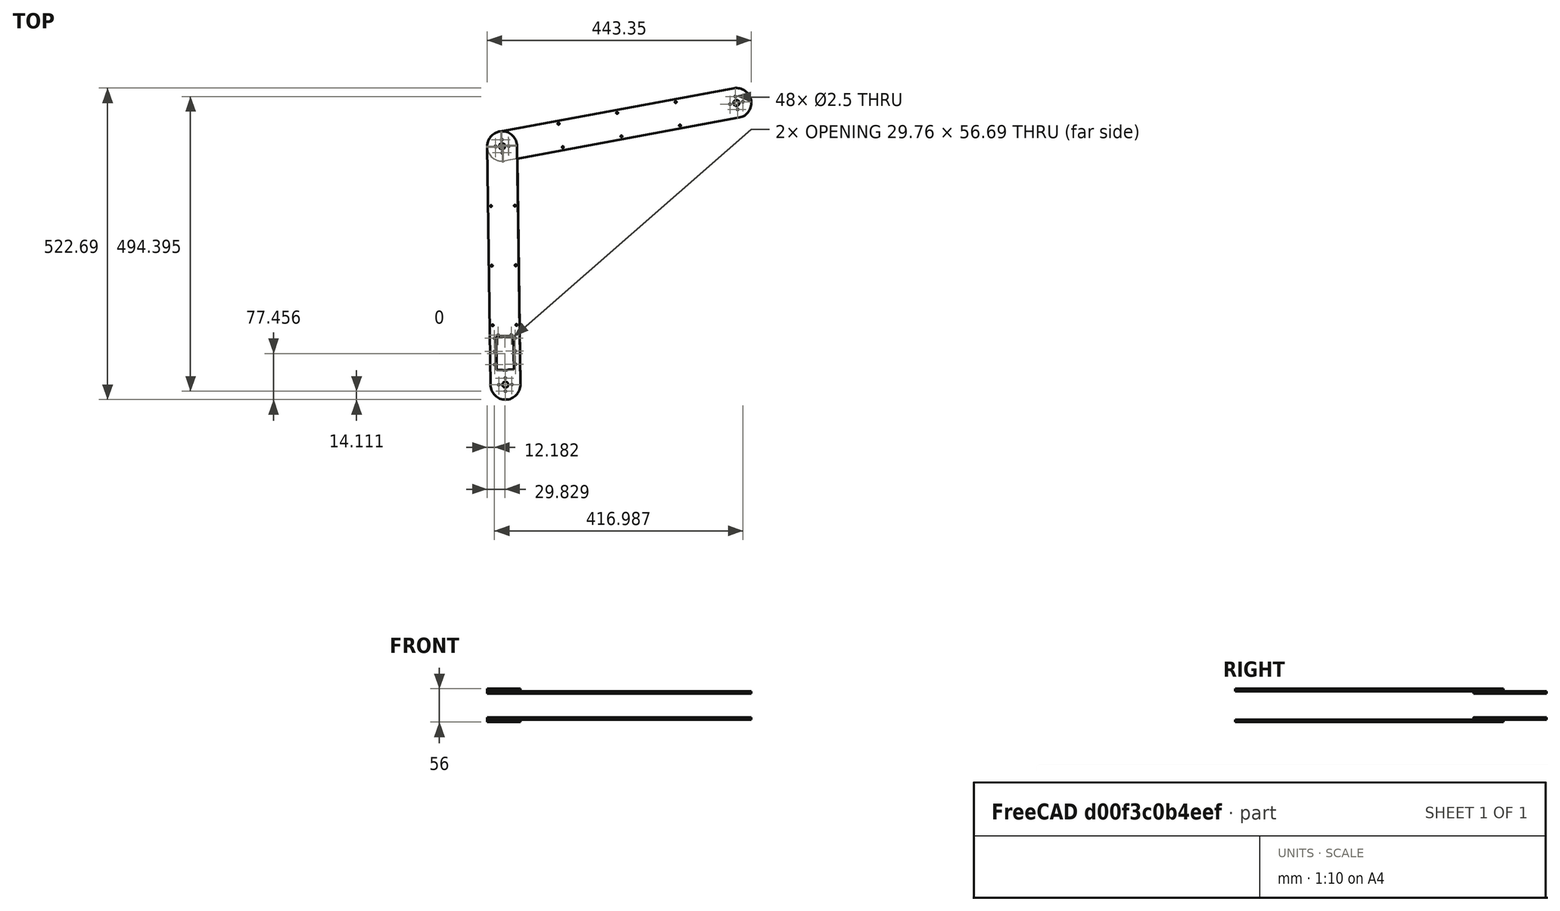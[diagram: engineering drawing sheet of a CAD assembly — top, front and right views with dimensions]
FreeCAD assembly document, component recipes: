
FREECAD ASSEMBLY — COMPONENT RECIPES ("arm_assembly_def")

This assembly document has 14 components, labeled P0..P13 below (a component is one placed body or linked part). 10 of them carry a construction recipe — the FreeCAD feature program that regenerates the part from scratch, quoted from this document or its linked companion documents; the rest are supplied as boundary geometry only. No exploded tour is included for this assembly.
COMPONENT P0 — recipe-attached ("arm_low_1", modeled in this document).
Construction recipe (the document's own serialized feature program — sketch geometry with constraints, then the solid features built on it; lengths are millimeters unless a unit is written):

FEATURE [Sketcher::SketchObject] Sketch
  ArcFitTolerance = 1e-06
  AttachmentSupport = -> [XY_Plane]
  FullyConstrained = false
  MakeInternals = false
  MapMode = 5
  sketch-geometry (67):
    g0: LineSegment [constr] StartX=1.5008e-12 StartY=20 StartZ=0 EndX=1.5008e-12 EndY=-20 EndZ=0
    g1: LineSegment [constr] StartX=-2.359e-12 StartY=0 StartZ=0 EndX=-2.359e-12 EndY=400 EndZ=0
    g2: LineSegment [constr] StartX=1.5008e-12 StartY=20 StartZ=0 EndX=1.5008e-12 EndY=25 EndZ=0
    g3: Circle CenterX=-2.359e-12 CenterY=400 CenterZ=0 NormalX=0 NormalY=0 NormalZ=1 AngleXU=0 Radius=5
    g4: Circle CenterX=-2.359e-12 CenterY=400 CenterZ=0 NormalX=0 NormalY=0 NormalZ=1 AngleXU=0 Radius=2
    g5: Circle CenterX=-10.9997 CenterY=400 CenterZ=0 NormalX=0 NormalY=0 NormalZ=1 AngleXU=0 Radius=1.25
    g6: Circle CenterX=0 CenterY=389 CenterZ=0 NormalX=0 NormalY=0 NormalZ=1 AngleXU=0 Radius=1.25
    g7: Circle CenterX=10.9997 CenterY=400 CenterZ=0 NormalX=0 NormalY=0 NormalZ=1 AngleXU=0 Radius=1.25
    g8: Circle CenterX=0 CenterY=411 CenterZ=0 NormalX=0 NormalY=0 NormalZ=1 AngleXU=0 Radius=1.25
    g9: LineSegment [constr] StartX=0 StartY=-5 StartZ=0 EndX=0 EndY=5.99996 EndZ=0
    g10: Circle [constr] CenterX=0 CenterY=0 CenterZ=0 NormalX=0 NormalY=0 NormalZ=1 AngleXU=0 Radius=14
    g11: LineSegment [constr] StartX=0 StartY=0 StartZ=0 EndX=25.23 EndY=0 EndZ=0
    g12: Circle [constr] CenterX=0 CenterY=-3.8e-05 CenterZ=0 NormalX=0 NormalY=0 NormalZ=1 AngleXU=0 Radius=11
    g13: Circle CenterX=0 CenterY=0 CenterZ=0 NormalX=0 NormalY=0 NormalZ=1 AngleXU=0 Radius=5
    g14: Circle CenterX=10.9997 CenterY=0 CenterZ=0 NormalX=0 NormalY=0 NormalZ=1 AngleXU=0 Radius=1.25
    g15: Circle CenterX=-10.9997 CenterY=0 CenterZ=0 NormalX=0 NormalY=0 NormalZ=1 AngleXU=0 Radius=1.25
    g16: Circle CenterX=0 CenterY=-10.9997 CenterZ=0 NormalX=0 NormalY=0 NormalZ=1 AngleXU=0 Radius=1.25
    g17: Circle CenterX=0 CenterY=11 CenterZ=0 NormalX=0 NormalY=0 NormalZ=1 AngleXU=0 Radius=1.25
    g18: LineSegment [constr] StartX=0 StartY=0 StartZ=0 EndX=-25 EndY=0 EndZ=0
    g19: LineSegment [constr] StartX=20.1368 StartY=86.0999 StartZ=0 EndX=20.1368 EndY=24.9999 EndZ=0
    g20: LineSegment [constr] StartX=0.036848 StartY=80.5 StartZ=0 EndX=14.5368 EndY=80.5 EndZ=0
    g21: LineSegment StartX=14.5368 StartY=80.5 StartZ=0 EndX=-14.4632 EndY=80.5 EndZ=0
    g22: LineSegment StartX=14.5368 StartY=80.5 StartZ=0 EndX=14.5368 EndY=24.9999 EndZ=0
    g23: Circle CenterX=11.0368 CenterY=83.3 CenterZ=0 NormalX=0 NormalY=0 NormalZ=1 AngleXU=0 Radius=1.25
    g24: Circle CenterX=17.3368 CenterY=78 CenterZ=0 NormalX=0 NormalY=0 NormalZ=1 AngleXU=0 Radius=1.25
    g25: LineSegment [constr] StartX=-20.0632 StartY=86.0999 StartZ=0 EndX=20.1368 EndY=86.0999 EndZ=0
    g26: Circle CenterX=17.3368 CenterY=56 CenterZ=0 NormalX=0 NormalY=0 NormalZ=1 AngleXU=0 Radius=1.25
    g27: Circle CenterX=17.3368 CenterY=34 CenterZ=0 NormalX=0 NormalY=0 NormalZ=1 AngleXU=0 Radius=1.25
    g28: Circle [constr] CenterX=0.036848 CenterY=37.9999 CenterZ=0 NormalX=0 NormalY=0 NormalZ=1 AngleXU=0 Radius=14
    g29: ArcOfCircle CenterX=0.036848 CenterY=37.9999 CenterZ=0 NormalX=0 NormalY=0 NormalZ=1 AngleXU=0 Radius=14 StartAngle=4.33214 EndAngle=5.09264
    g30: LineSegment StartX=5.233 StartY=24.9999 StartZ=0 EndX=14.5368 EndY=24.9999 EndZ=0
    g31: LineSegment [constr] StartX=14.5368 StartY=24.9999 StartZ=0 EndX=20.1368 EndY=24.9999 EndZ=0
    g32: LineSegment [constr] StartX=17.3368 StartY=56 StartZ=0 EndX=-17.2632 EndY=56 EndZ=0
    g33: LineSegment [constr] StartX=-20.0632 StartY=24.9999 StartZ=0 EndX=-20.0632 EndY=86.0999 EndZ=0
    g34: LineSegment StartX=-14.4632 StartY=80.5 StartZ=0 EndX=-14.4632 EndY=24.9999 EndZ=0
    g35: Circle CenterX=-17.2632 CenterY=78 CenterZ=0 NormalX=0 NormalY=0 NormalZ=1 AngleXU=0 Radius=1.25
    g36: Circle CenterX=-10.9632 CenterY=83.3 CenterZ=0 NormalX=0 NormalY=0 NormalZ=1 AngleXU=0 Radius=1.25
    g37: Circle CenterX=-17.2632 CenterY=56 CenterZ=0 NormalX=0 NormalY=0 NormalZ=1 AngleXU=0 Radius=1.25
    g38: Circle CenterX=-17.2632 CenterY=34 CenterZ=0 NormalX=0 NormalY=0 NormalZ=1 AngleXU=0 Radius=1.25
    g39: LineSegment StartX=-14.4632 StartY=24.9999 StartZ=0 EndX=-5.15931 EndY=24.9999 EndZ=0
    g40: LineSegment [constr] StartX=-20.0632 StartY=24.9999 StartZ=0 EndX=-14.4632 EndY=24.9999 EndZ=0
    g41: ArcOfCircle CenterX=0.115002 CenterY=3.75548e-06 CenterZ=0 NormalX=0 NormalY=0 NormalZ=1 AngleXU=0 Radius=25.115 StartAngle=3.14159 EndAngle=6.28319
    g42: ArcOfCircle CenterX=0.115002 CenterY=399.959 CenterZ=0 NormalX=0 NormalY=0 NormalZ=1 AngleXU=0 Radius=25.115 StartAngle=0 EndAngle=3.14159
    g43: LineSegment StartX=-25 StartY=3.75548e-06 StartZ=0 EndX=-25 EndY=399.959 EndZ=0
    g44: LineSegment StartX=25.23 StartY=3.75548e-06 StartZ=0 EndX=25.23 EndY=399.959 EndZ=0
    g45: LineSegment [constr] StartX=25.23 StartY=199.98 StartZ=0 EndX=-25 EndY=199.98 EndZ=0
    g46: LineSegment [constr] StartX=25.23 StartY=199.98 StartZ=0 EndX=55.23 EndY=199.98 EndZ=0
    g47: LineSegment [constr] StartX=25.23 StartY=0 StartZ=0 EndX=55.23 EndY=0 EndZ=0
    g48: LineSegment [constr] StartX=55.23 StartY=0 StartZ=0 EndX=55.23 EndY=199.98 EndZ=0
    g49: LineSegment [constr] StartX=55.23 StartY=99.9898 StartZ=0 EndX=25.23 EndY=99.9898 EndZ=0
    g50: LineSegment [constr] StartX=25.23 StartY=99.9898 StartZ=0 EndX=-25 EndY=99.9898 EndZ=0
    g51: LineSegment [constr] StartX=25.23 StartY=399.959 StartZ=0 EndX=55.23 EndY=399.959 EndZ=0
    g52: LineSegment [constr] StartX=55.23 StartY=399.959 StartZ=0 EndX=55.23 EndY=199.98 EndZ=0
    g53: LineSegment [constr] StartX=55.23 StartY=299.969 StartZ=0 EndX=25.23 EndY=299.969 EndZ=0
    g54: LineSegment [constr] StartX=25.23 StartY=299.969 StartZ=0 EndX=-25 EndY=299.969 EndZ=0
    g55: LineSegment [constr] StartX=-25 StartY=299.969 StartZ=0 EndX=-20 EndY=299.969 EndZ=0
    g56: LineSegment [constr] StartX=-20 StartY=299.969 StartZ=0 EndX=-20 EndY=199.98 EndZ=0
    g57: LineSegment [constr] StartX=-20 StartY=199.98 StartZ=0 EndX=-20 EndY=99.9898 EndZ=0
    g58: LineSegment [constr] StartX=25.23 StartY=299.969 StartZ=0 EndX=20.23 EndY=299.969 EndZ=0
    g59: LineSegment [constr] StartX=20.23 StartY=299.969 StartZ=0 EndX=20.23 EndY=199.98 EndZ=0
    g60: LineSegment [constr] StartX=20.23 StartY=199.98 StartZ=0 EndX=20.23 EndY=99.9898 EndZ=0
    g61: Circle CenterX=-20 CenterY=299.969 CenterZ=0 NormalX=0 NormalY=0 NormalZ=1 AngleXU=0 Radius=1.5
    g62: Circle CenterX=20.23 CenterY=299.969 CenterZ=0 NormalX=0 NormalY=0 NormalZ=1 AngleXU=0 Radius=1.5
    g63: Circle CenterX=-20 CenterY=199.98 CenterZ=0 NormalX=0 NormalY=0 NormalZ=1 AngleXU=0 Radius=1.5
    g64: Circle CenterX=20.23 CenterY=199.98 CenterZ=0 NormalX=0 NormalY=0 NormalZ=1 AngleXU=0 Radius=1.5
    g65: Circle CenterX=-20 CenterY=99.9898 CenterZ=0 NormalX=0 NormalY=0 NormalZ=1 AngleXU=0 Radius=1.5
    g66: Circle CenterX=20.23 CenterY=99.9898 CenterZ=0 NormalX=0 NormalY=0 NormalZ=1 AngleXU=0 Radius=1.5
  constraints (132):
    c: Vertical(g0)
    c: Vertical(g1)
    c: Coincident(g2,g0)
    c: Vertical(g2)
    c: Diameter(g3) = 10
    c: Coincident(g3,g1)
    c: Diameter(g4) = 4
    c: Coincident(g4,g1)
    c: Diameter(g8) = 2.5
    c: Diameter(g5) = 2.5
    c: Diameter(g6) = 2.5
    c: Diameter(g7) = 2.5
    c: Vertical(g9)
    c: Diameter(g10) = 28
    c: Coincident(g18,g10)
    c: Horizontal(g18)
    c: Coincident(g11,g10)
    c: Horizontal(g11)
    c: Diameter(g12) = 22
    c: Diameter(g13) = 10
    c: Coincident(g13,g10)
    c: Diameter(g17) = 2.5
    c: Diameter(g15) = 2.5
    c: Diameter(g16) = 2.5
    c: Diameter(g14) = 2.5
    c: Coincident(g25,g19)
    c: Coincident(g33,g25)
    c: Horizontal(g25)
    c: Vertical(g19)
    c: Vertical(g33)
    c: Distance(g19,g33) = 40.2
    c: Distance(g25,g33) = 61.1
    c: Diameter(g29) = 28
    c: Horizontal(g20)
    c: Coincident(g21,g20)
    c: Horizontal(g21)
    c: Coincident(g34,g21)
    c: Vertical(g34)
    c: Coincident(g22,g20)
    c: Vertical(g22)
    c: Diameter(g23) = 2.5
    c: Equal(g23,g36)
    c: Equal(g23,g27)
    c: Equal(g23,g38)
    c: Equal(g23,g37)
    c: Equal(g23,g35)
    c: Equal(g23,g24)
    c: Equal(g23,g26)
    c: Coincident(g28,g29)
    c: PointOnObject(g29,g28)
    c: Coincident(g30,g29)
    c: Coincident(g30,g22)
    c: Horizontal(g30)
    c: Coincident(g31,g22)
    c: Coincident(g31,g19)
    c: Horizontal(g31)
    c: Coincident(g39,g34)
    c: Coincident(g39,g29)
    c: Horizontal(g39)
    c: Coincident(g40,g33)
    c: Coincident(g40,g34)
    c: Horizontal(g40)
    c: Coincident(g32,g26)
    c: Coincident(g32,g37)
    c: Horizontal(g32)
    c: DistanceY(g28,g1) = 362
    c: Tangent(g41,g43) = 1.5708
    c: Tangent(g41,g44) = -1.5708
    c: Tangent(g42,g43) = 1.5708
    c: Tangent(g42,g44) = -1.5708
    c: Equal(g41,g42)
    c: Symmetric(g44,g44,g45)
    c: Symmetric(g43,g43,g45)
    c: Horizontal(g45)
    c: Distance(g46) = 30
    c: Horizontal(g46)
    c: Coincident(g46,g45)
    c: Distance(g47) = 30
    c: Horizontal(g47)
    c: Coincident(g47,g11)
    c: PointOnObject(g47,g-1)
    c: Coincident(g48,g47)
    c: Coincident(g48,g46)
    c: Vertical(g48)
    c: Symmetric(g48,g48,g49)
    c: PointOnObject(g49,g44)
    c: Horizontal(g49)
    c: Coincident(g50,g49)
    c: PointOnObject(g50,g43)
    c: Horizontal(g50)
    c: Distance(g51) = 30
    c: Horizontal(g51)
    c: Coincident(g51,g42)
    c: Coincident(g52,g51)
    c: Coincident(g52,g46)
    c: Symmetric(g52,g52,g53)
    c: PointOnObject(g53,g44)
    c: Horizontal(g53)
    c: Coincident(g54,g53)
    c: PointOnObject(g54,g43)
    c: Horizontal(g54)
    c: Distance(g55) = 5
    c: Coincident(g55,g54)
    c: PointOnObject(g55,g54)
    c: Coincident(g56,g55)
    c: PointOnObject(g56,g45)
    c: Vertical(g56)
    c: Coincident(g57,g56)
    c: PointOnObject(g57,g50)
    c: Vertical(g57)
    c: Distance(g58) = 5
    c: Coincident(g58,g53)
    c: PointOnObject(g58,g54)
    c: Coincident(g59,g58)
    c: PointOnObject(g59,g45)
    c: Vertical(g59)
    c: Coincident(g60,g59)
    c: PointOnObject(g60,g50)
    c: Vertical(g60)
    c: Coincident(g61,g55)
    c: Diameter(g61) = 3
    c: Coincident(g62,g58)
    c: Equal(g61,g62)
    c: Coincident(g63,g56)
    c: Equal(g61,g63)
    c: Coincident(g64,g59)
    c: Equal(g63,g64)
    c: Coincident(g65,g57)
    c: Equal(g63,g65)
    c: Coincident(g66,g60)
    c: Equal(g65,g66)
    c: DistanceY(g41,g28) = 37.9999
FEATURE [PartDesign::Pad] Pad
  Direction = (0,0,1)
  Length = 4
  Length2 = 10
  Profile = -> Sketch
  ReferenceAxis = -> Sketch [N_Axis]
  Refine = true
  Suppressed = false
  Type = 0
FEATURE [PartDesign::Body] Body  label="arm_low_1"
  AllowCompound = false
  Group = -> [Sketch,Pad]
  Origin = -> Origin
  Placement = pos=(0,0,25.3) rot=(0,0,1;0.013804rad)
  Tip = -> Pad
COMPONENT P1 — recipe-attached ("arm_high_1", modeled in this document).
Construction recipe (the document's own serialized feature program — sketch geometry with constraints, then the solid features built on it; lengths are millimeters unless a unit is written):

FEATURE [Sketcher::SketchObject] Sketch001
  ArcFitTolerance = 1e-06
  FullyConstrained = false
  MakeInternals = false
  MapMode = 5
  sketch-geometry (41):
    g0: Circle [constr] CenterX=7e-16 CenterY=0.000303 CenterZ=0 NormalX=0 NormalY=0 NormalZ=1 AngleXU=0 Radius=14
    g1: LineSegment [constr] StartX=7e-16 StartY=0.000303 StartZ=0 EndX=7e-16 EndY=400.001 EndZ=0
    g2: Circle CenterX=7e-16 CenterY=400.001 CenterZ=0 NormalX=0 NormalY=0 NormalZ=1 AngleXU=0 Radius=5
    g3: Circle CenterX=7e-16 CenterY=0 CenterZ=0 NormalX=0 NormalY=0 NormalZ=1 AngleXU=0 Radius=5
    g4: Circle CenterX=7e-16 CenterY=400.001 CenterZ=0 NormalX=0 NormalY=0 NormalZ=1 AngleXU=0 Radius=2
    g5: Circle CenterX=7e-16 CenterY=0.000303 CenterZ=0 NormalX=0 NormalY=0 NormalZ=1 AngleXU=0 Radius=2
    g6: Circle [constr] CenterX=0 CenterY=0 CenterZ=0 NormalX=0 NormalY=0 NormalZ=1 AngleXU=0 Radius=11
    g7: ArcOfCircle CenterX=7e-16 CenterY=0 CenterZ=0 NormalX=0 NormalY=0 NormalZ=1 AngleXU=0 Radius=25 StartAngle=3.14159 EndAngle=6.28319
    g8: ArcOfCircle CenterX=7e-16 CenterY=400.001 CenterZ=0 NormalX=0 NormalY=0 NormalZ=1 AngleXU=0 Radius=25 StartAngle=6e-16 EndAngle=3.14159
    g9: LineSegment StartX=-25 StartY=-8e-15 StartZ=0 EndX=-25 EndY=400.001 EndZ=0
    g10: LineSegment StartX=25 StartY=0 StartZ=0 EndX=25 EndY=400.001 EndZ=0
    g11: Circle CenterX=10.9997 CenterY=400.001 CenterZ=0 NormalX=0 NormalY=0 NormalZ=1 AngleXU=0 Radius=1.25
    g12: Circle CenterX=0 CenterY=411.001 CenterZ=0 NormalX=0 NormalY=0 NormalZ=1 AngleXU=0 Radius=1.25
    g13: Circle CenterX=-10.9997 CenterY=400.001 CenterZ=0 NormalX=0 NormalY=0 NormalZ=1 AngleXU=0 Radius=1.25
    g14: Circle CenterX=0 CenterY=389.001 CenterZ=0 NormalX=0 NormalY=0 NormalZ=1 AngleXU=0 Radius=1.25
    g15: Circle CenterX=10.9997 CenterY=0.000303 CenterZ=0 NormalX=0 NormalY=0 NormalZ=1 AngleXU=0 Radius=1.25
    g16: Circle CenterX=0 CenterY=11 CenterZ=0 NormalX=0 NormalY=0 NormalZ=1 AngleXU=0 Radius=1.25
    g17: Circle CenterX=-10.9997 CenterY=0.000303 CenterZ=0 NormalX=0 NormalY=0 NormalZ=1 AngleXU=0 Radius=1.25
    g18: Circle CenterX=0 CenterY=-10.9994 CenterZ=0 NormalX=0 NormalY=0 NormalZ=1 AngleXU=0 Radius=1.25
    g19: LineSegment [constr] StartX=25 StartY=200 StartZ=0 EndX=-25 EndY=200 EndZ=0
    g20: LineSegment [constr] StartX=25 StartY=200 StartZ=0 EndX=55 EndY=200 EndZ=0
    g21: LineSegment [constr] StartX=25 StartY=0 StartZ=0 EndX=55 EndY=0 EndZ=0
    g22: LineSegment [constr] StartX=25 StartY=400.001 StartZ=0 EndX=55 EndY=400.001 EndZ=0
    g23: LineSegment [constr] StartX=55 StartY=200 StartZ=0 EndX=55 EndY=400.001 EndZ=0
    g24: LineSegment [constr] StartX=55 StartY=200 StartZ=0 EndX=55 EndY=0 EndZ=0
    g25: LineSegment [constr] StartX=55 StartY=100 StartZ=0 EndX=25 EndY=100 EndZ=0
    g26: LineSegment [constr] StartX=25 StartY=100 StartZ=0 EndX=-25 EndY=100 EndZ=0
    g27: LineSegment [constr] StartX=55 StartY=300 StartZ=0 EndX=25 EndY=300 EndZ=0
    g28: LineSegment [constr] StartX=25 StartY=300 StartZ=0 EndX=-25 EndY=300 EndZ=0
    g29: LineSegment [constr] StartX=-25 StartY=300 StartZ=0 EndX=-20 EndY=300 EndZ=0
    g30: LineSegment [constr] StartX=-20 StartY=300 StartZ=0 EndX=-20 EndY=200 EndZ=0
    g31: LineSegment [constr] StartX=-20 StartY=200 StartZ=0 EndX=-20 EndY=100 EndZ=0
    g32: LineSegment [constr] StartX=25 StartY=100 StartZ=0 EndX=20 EndY=100 EndZ=0
    g33: LineSegment [constr] StartX=20 StartY=100 StartZ=0 EndX=20 EndY=200 EndZ=0
    g34: LineSegment [constr] StartX=20 StartY=200 StartZ=0 EndX=20 EndY=300 EndZ=0
    g35: Circle CenterX=-20 CenterY=300 CenterZ=0 NormalX=0 NormalY=0 NormalZ=1 AngleXU=0 Radius=1.5
    g36: Circle CenterX=20 CenterY=300 CenterZ=0 NormalX=0 NormalY=0 NormalZ=1 AngleXU=0 Radius=1.5
    g37: Circle CenterX=-20 CenterY=200 CenterZ=0 NormalX=0 NormalY=0 NormalZ=1 AngleXU=0 Radius=1.5
    g38: Circle CenterX=20 CenterY=200 CenterZ=0 NormalX=0 NormalY=0 NormalZ=1 AngleXU=0 Radius=1.5
    g39: Circle CenterX=-20 CenterY=100 CenterZ=0 NormalX=0 NormalY=0 NormalZ=1 AngleXU=0 Radius=1.5
    g40: Circle CenterX=20 CenterY=100 CenterZ=0 NormalX=0 NormalY=0 NormalZ=1 AngleXU=0 Radius=1.5
  constraints (85):
    c: Diameter(g0) = 28
    c: Coincident(g1,g0)
    c: Vertical(g1)
    c: Coincident(g2,g1)
    c: Diameter(g3) = 10
    c: Diameter(g4) = 4
    c: Coincident(g4,g1)
    c: Diameter(g5) = 4
    c: Coincident(g5,g0)
    c: Diameter(g6) = 22
    c: Tangent(g7,g9) = 1.5708
    c: Tangent(g7,g10) = -1.5708
    c: Tangent(g8,g9) = 1.5708
    c: Tangent(g8,g10) = -1.5708
    c: Equal(g7,g8)
    c: Radius(g7) = 25
    c: Coincident(g7,g3)
    c: Coincident(g8,g1)
    c: Vertical(g9)
    c: Diameter(g12) = 2.5
    c: Diameter(g13) = 2.5
    c: Diameter(g14) = 2.5
    c: Diameter(g11) = 2.5
    c: Diameter(g16) = 2.5
    c: Diameter(g17) = 2.5
    c: Diameter(g18) = 2.5
    c: Diameter(g15) = 2.5
    c: Symmetric(g10,g10,g19)
    c: Symmetric(g9,g9,g19)
    c: Distance(g20) = 30
    c: Horizontal(g20)
    c: Coincident(g20,g19)
    c: Distance(g21) = 30
    c: Horizontal(g21)
    c: Coincident(g21,g7)
    c: PointOnObject(g21,g-1)
    c: Distance(g22) = 30
    c: Horizontal(g22)
    c: Coincident(g22,g8)
    c: Coincident(g23,g20)
    c: Coincident(g23,g22)
    c: Coincident(g24,g20)
    c: Coincident(g24,g21)
    c: Symmetric(g24,g24,g25)
    c: PointOnObject(g25,g10)
    c: Horizontal(g25)
    c: Coincident(g26,g25)
    c: PointOnObject(g26,g9)
    c: Horizontal(g26)
    c: Symmetric(g23,g23,g27)
    c: PointOnObject(g27,g10)
    c: Horizontal(g27)
    c: Coincident(g28,g27)
    c: PointOnObject(g28,g9)
    c: Horizontal(g28)
    c: Distance(g29) = 5
    c: Horizontal(g29)
    c: Coincident(g29,g28)
    c: Coincident(g30,g29)
    c: PointOnObject(g30,g19)
    c: Vertical(g30)
    c: Coincident(g31,g30)
    c: PointOnObject(g31,g26)
    c: Vertical(g31)
    c: Distance(g32) = 5
    c: Horizontal(g32)
    c: Coincident(g32,g25)
    c: Coincident(g33,g32)
    c: PointOnObject(g33,g19)
    c: Vertical(g33)
    c: Coincident(g34,g33)
    c: PointOnObject(g34,g28)
    c: Vertical(g34)
    c: Diameter(g35) = 3
    c: Coincident(g35,g29)
    c: Coincident(g36,g34)
    c: Equal(g35,g36)
    c: Coincident(g37,g30)
    c: Equal(g35,g37)
    c: Coincident(g38,g33)
    c: Equal(g37,g38)
    c: Coincident(g39,g31)
    c: Equal(g37,g39)
    c: Coincident(g40,g32)
    c: Equal(g39,g40)
FEATURE [PartDesign::Pad] Pad001
  Direction = (0,0,1)
  Length = 4
  Length2 = 10
  Profile = -> Sketch001
  ReferenceAxis = -> Sketch001 [N_Axis]
  Refine = true
  Suppressed = false
  Type = 0
FEATURE [PartDesign::Body] Body001  label="arm_high_1"
  AllowCompound = false
  Group = -> [Sketch001,Pad001]
  Origin = -> Origin001
  Placement = pos=(387.832,472.58,29.3) rot=(0,0,1;1.75335rad)
  Tip = -> Pad001
COMPONENT P2 — same part as P0; its construction recipe is shown at P0.
COMPONENT P3 — same part as P0; its construction recipe is shown at P0.
COMPONENT P4 — recipe-attached ("arm_low_002", modeled in this document).
Construction recipe (the document's own serialized feature program — sketch geometry with constraints, then the solid features built on it; lengths are millimeters unless a unit is written):

FEATURE [Sketcher::SketchObject] Sketch002
  ArcFitTolerance = 1e-06
  AttachmentSupport = -> [XY_Plane004]
  FullyConstrained = false
  MakeInternals = false
  MapMode = 5
  sketch-geometry (67):
    g0: LineSegment [constr] StartX=1.5008e-12 StartY=20 StartZ=0 EndX=1.5008e-12 EndY=-20 EndZ=0
    g1: LineSegment [constr] StartX=-2.359e-12 StartY=0 StartZ=0 EndX=-2.359e-12 EndY=400 EndZ=0
    g2: LineSegment [constr] StartX=1.5008e-12 StartY=20 StartZ=0 EndX=1.5008e-12 EndY=25 EndZ=0
    g3: Circle CenterX=-2.359e-12 CenterY=400 CenterZ=0 NormalX=0 NormalY=0 NormalZ=1 AngleXU=0 Radius=5
    g4: Circle CenterX=-2.359e-12 CenterY=400 CenterZ=0 NormalX=0 NormalY=0 NormalZ=1 AngleXU=0 Radius=2
    g5: Circle CenterX=-10.9997 CenterY=400 CenterZ=0 NormalX=0 NormalY=0 NormalZ=1 AngleXU=0 Radius=1.25
    g6: Circle CenterX=0 CenterY=389 CenterZ=0 NormalX=0 NormalY=0 NormalZ=1 AngleXU=0 Radius=1.25
    g7: Circle CenterX=10.9997 CenterY=400 CenterZ=0 NormalX=0 NormalY=0 NormalZ=1 AngleXU=0 Radius=1.25
    g8: Circle CenterX=0 CenterY=411 CenterZ=0 NormalX=0 NormalY=0 NormalZ=1 AngleXU=0 Radius=1.25
    g9: LineSegment [constr] StartX=0 StartY=-5 StartZ=0 EndX=0 EndY=5.99996 EndZ=0
    g10: Circle [constr] CenterX=0 CenterY=0 CenterZ=0 NormalX=0 NormalY=0 NormalZ=1 AngleXU=0 Radius=14
    g11: LineSegment [constr] StartX=0 StartY=0 StartZ=0 EndX=25.23 EndY=0 EndZ=0
    g12: Circle [constr] CenterX=0 CenterY=-3.8e-05 CenterZ=0 NormalX=0 NormalY=0 NormalZ=1 AngleXU=0 Radius=11
    g13: Circle CenterX=0 CenterY=0 CenterZ=0 NormalX=0 NormalY=0 NormalZ=1 AngleXU=0 Radius=5
    g14: Circle CenterX=10.9997 CenterY=0 CenterZ=0 NormalX=0 NormalY=0 NormalZ=1 AngleXU=0 Radius=1.25
    g15: Circle CenterX=-10.9997 CenterY=0 CenterZ=0 NormalX=0 NormalY=0 NormalZ=1 AngleXU=0 Radius=1.25
    g16: Circle CenterX=0 CenterY=-10.9997 CenterZ=0 NormalX=0 NormalY=0 NormalZ=1 AngleXU=0 Radius=1.25
    g17: Circle CenterX=0 CenterY=11 CenterZ=0 NormalX=0 NormalY=0 NormalZ=1 AngleXU=0 Radius=1.25
    g18: LineSegment [constr] StartX=0 StartY=0 StartZ=0 EndX=-25 EndY=0 EndZ=0
    g19: LineSegment [constr] StartX=20.1368 StartY=86.0999 StartZ=0 EndX=20.1368 EndY=24.9999 EndZ=0
    g20: LineSegment [constr] StartX=0.036848 StartY=80.5 StartZ=0 EndX=14.5368 EndY=80.5 EndZ=0
    g21: LineSegment StartX=14.5368 StartY=80.5 StartZ=0 EndX=-14.4632 EndY=80.5 EndZ=0
    g22: LineSegment StartX=14.5368 StartY=80.5 StartZ=0 EndX=14.5368 EndY=24.9999 EndZ=0
    g23: Circle CenterX=11.0368 CenterY=83.3 CenterZ=0 NormalX=0 NormalY=0 NormalZ=1 AngleXU=0 Radius=1.25
    g24: Circle CenterX=17.3368 CenterY=78 CenterZ=0 NormalX=0 NormalY=0 NormalZ=1 AngleXU=0 Radius=1.25
    g25: LineSegment [constr] StartX=-20.0632 StartY=86.0999 StartZ=0 EndX=20.1368 EndY=86.0999 EndZ=0
    g26: Circle CenterX=17.3368 CenterY=56 CenterZ=0 NormalX=0 NormalY=0 NormalZ=1 AngleXU=0 Radius=1.25
    g27: Circle CenterX=17.3368 CenterY=34 CenterZ=0 NormalX=0 NormalY=0 NormalZ=1 AngleXU=0 Radius=1.25
    g28: Circle [constr] CenterX=0.036848 CenterY=37.9999 CenterZ=0 NormalX=0 NormalY=0 NormalZ=1 AngleXU=0 Radius=14
    g29: ArcOfCircle CenterX=0.036848 CenterY=37.9999 CenterZ=0 NormalX=0 NormalY=0 NormalZ=1 AngleXU=0 Radius=14 StartAngle=4.33214 EndAngle=5.09264
    g30: LineSegment StartX=5.233 StartY=24.9999 StartZ=0 EndX=14.5368 EndY=24.9999 EndZ=0
    g31: LineSegment [constr] StartX=14.5368 StartY=24.9999 StartZ=0 EndX=20.1368 EndY=24.9999 EndZ=0
    g32: LineSegment [constr] StartX=17.3368 StartY=56 StartZ=0 EndX=-17.2632 EndY=56 EndZ=0
    g33: LineSegment [constr] StartX=-20.0632 StartY=24.9999 StartZ=0 EndX=-20.0632 EndY=86.0999 EndZ=0
    g34: LineSegment StartX=-14.4632 StartY=80.5 StartZ=0 EndX=-14.4632 EndY=24.9999 EndZ=0
    g35: Circle CenterX=-17.2632 CenterY=78 CenterZ=0 NormalX=0 NormalY=0 NormalZ=1 AngleXU=0 Radius=1.25
    g36: Circle CenterX=-10.9632 CenterY=83.3 CenterZ=0 NormalX=0 NormalY=0 NormalZ=1 AngleXU=0 Radius=1.25
    g37: Circle CenterX=-17.2632 CenterY=56 CenterZ=0 NormalX=0 NormalY=0 NormalZ=1 AngleXU=0 Radius=1.25
    g38: Circle CenterX=-17.2632 CenterY=34 CenterZ=0 NormalX=0 NormalY=0 NormalZ=1 AngleXU=0 Radius=1.25
    g39: LineSegment StartX=-14.4632 StartY=24.9999 StartZ=0 EndX=-5.15931 EndY=24.9999 EndZ=0
    g40: LineSegment [constr] StartX=-20.0632 StartY=24.9999 StartZ=0 EndX=-14.4632 EndY=24.9999 EndZ=0
    g41: ArcOfCircle CenterX=0.115002 CenterY=3.75548e-06 CenterZ=0 NormalX=0 NormalY=0 NormalZ=1 AngleXU=0 Radius=25.115 StartAngle=3.14159 EndAngle=6.28319
    g42: ArcOfCircle CenterX=0.115002 CenterY=399.959 CenterZ=0 NormalX=0 NormalY=0 NormalZ=1 AngleXU=0 Radius=25.115 StartAngle=0 EndAngle=3.14159
    g43: LineSegment StartX=-25 StartY=3.75548e-06 StartZ=0 EndX=-25 EndY=399.959 EndZ=0
    g44: LineSegment StartX=25.23 StartY=3.75548e-06 StartZ=0 EndX=25.23 EndY=399.959 EndZ=0
    g45: LineSegment [constr] StartX=25.23 StartY=199.98 StartZ=0 EndX=-25 EndY=199.98 EndZ=0
    g46: LineSegment [constr] StartX=25.23 StartY=199.98 StartZ=0 EndX=55.23 EndY=199.98 EndZ=0
    g47: LineSegment [constr] StartX=25.23 StartY=0 StartZ=0 EndX=55.23 EndY=0 EndZ=0
    g48: LineSegment [constr] StartX=55.23 StartY=0 StartZ=0 EndX=55.23 EndY=199.98 EndZ=0
    g49: LineSegment [constr] StartX=55.23 StartY=99.9898 StartZ=0 EndX=25.23 EndY=99.9898 EndZ=0
    g50: LineSegment [constr] StartX=25.23 StartY=99.9898 StartZ=0 EndX=-25 EndY=99.9898 EndZ=0
    g51: LineSegment [constr] StartX=25.23 StartY=399.959 StartZ=0 EndX=55.23 EndY=399.959 EndZ=0
    g52: LineSegment [constr] StartX=55.23 StartY=399.959 StartZ=0 EndX=55.23 EndY=199.98 EndZ=0
    g53: LineSegment [constr] StartX=55.23 StartY=299.969 StartZ=0 EndX=25.23 EndY=299.969 EndZ=0
    g54: LineSegment [constr] StartX=25.23 StartY=299.969 StartZ=0 EndX=-25 EndY=299.969 EndZ=0
    g55: LineSegment [constr] StartX=-25 StartY=299.969 StartZ=0 EndX=-20 EndY=299.969 EndZ=0
    g56: LineSegment [constr] StartX=-20 StartY=299.969 StartZ=0 EndX=-20 EndY=199.98 EndZ=0
    g57: LineSegment [constr] StartX=-20 StartY=199.98 StartZ=0 EndX=-20 EndY=99.9898 EndZ=0
    g58: LineSegment [constr] StartX=25.23 StartY=299.969 StartZ=0 EndX=20.23 EndY=299.969 EndZ=0
    g59: LineSegment [constr] StartX=20.23 StartY=299.969 StartZ=0 EndX=20.23 EndY=199.98 EndZ=0
    g60: LineSegment [constr] StartX=20.23 StartY=199.98 StartZ=0 EndX=20.23 EndY=99.9898 EndZ=0
    g61: Circle CenterX=-20 CenterY=299.969 CenterZ=0 NormalX=0 NormalY=0 NormalZ=1 AngleXU=0 Radius=1.5
    g62: Circle CenterX=20.23 CenterY=299.969 CenterZ=0 NormalX=0 NormalY=0 NormalZ=1 AngleXU=0 Radius=1.5
    g63: Circle CenterX=-20 CenterY=199.98 CenterZ=0 NormalX=0 NormalY=0 NormalZ=1 AngleXU=0 Radius=1.5
    g64: Circle CenterX=20.23 CenterY=199.98 CenterZ=0 NormalX=0 NormalY=0 NormalZ=1 AngleXU=0 Radius=1.5
    g65: Circle CenterX=-20 CenterY=99.9898 CenterZ=0 NormalX=0 NormalY=0 NormalZ=1 AngleXU=0 Radius=1.5
    g66: Circle CenterX=20.23 CenterY=99.9898 CenterZ=0 NormalX=0 NormalY=0 NormalZ=1 AngleXU=0 Radius=1.5
  constraints (132):
    c: Vertical(g0)
    c: Vertical(g1)
    c: Coincident(g2,g0)
    c: Vertical(g2)
    c: Diameter(g3) = 10
    c: Coincident(g3,g1)
    c: Diameter(g4) = 4
    c: Coincident(g4,g1)
    c: Diameter(g8) = 2.5
    c: Diameter(g5) = 2.5
    c: Diameter(g6) = 2.5
    c: Diameter(g7) = 2.5
    c: Vertical(g9)
    c: Diameter(g10) = 28
    c: Coincident(g18,g10)
    c: Horizontal(g18)
    c: Coincident(g11,g10)
    c: Horizontal(g11)
    c: Diameter(g12) = 22
    c: Diameter(g13) = 10
    c: Coincident(g13,g10)
    c: Diameter(g17) = 2.5
    c: Diameter(g15) = 2.5
    c: Diameter(g16) = 2.5
    c: Diameter(g14) = 2.5
    c: Coincident(g25,g19)
    c: Coincident(g33,g25)
    c: Horizontal(g25)
    c: Vertical(g19)
    c: Vertical(g33)
    c: Distance(g19,g33) = 40.2
    c: Distance(g25,g33) = 61.1
    c: Diameter(g29) = 28
    c: Horizontal(g20)
    c: Coincident(g21,g20)
    c: Horizontal(g21)
    c: Coincident(g34,g21)
    c: Vertical(g34)
    c: Coincident(g22,g20)
    c: Vertical(g22)
    c: Diameter(g23) = 2.5
    c: Equal(g23,g36)
    c: Equal(g23,g27)
    c: Equal(g23,g38)
    c: Equal(g23,g37)
    c: Equal(g23,g35)
    c: Equal(g23,g24)
    c: Equal(g23,g26)
    c: Coincident(g28,g29)
    c: PointOnObject(g29,g28)
    c: Coincident(g30,g29)
    c: Coincident(g30,g22)
    c: Horizontal(g30)
    c: Coincident(g31,g22)
    c: Coincident(g31,g19)
    c: Horizontal(g31)
    c: Coincident(g39,g34)
    c: Coincident(g39,g29)
    c: Horizontal(g39)
    c: Coincident(g40,g33)
    c: Coincident(g40,g34)
    c: Horizontal(g40)
    c: Coincident(g32,g26)
    c: Coincident(g32,g37)
    c: Horizontal(g32)
    c: DistanceY(g28,g1) = 362
    c: Tangent(g41,g43) = 1.5708
    c: Tangent(g41,g44) = -1.5708
    c: Tangent(g42,g43) = 1.5708
    c: Tangent(g42,g44) = -1.5708
    c: Equal(g41,g42)
    c: Symmetric(g44,g44,g45)
    c: Symmetric(g43,g43,g45)
    c: Horizontal(g45)
    c: Distance(g46) = 30
    c: Horizontal(g46)
    c: Coincident(g46,g45)
    c: Distance(g47) = 30
    c: Horizontal(g47)
    c: Coincident(g47,g11)
    c: PointOnObject(g47,g-1)
    c: Coincident(g48,g47)
    c: Coincident(g48,g46)
    c: Vertical(g48)
    c: Symmetric(g48,g48,g49)
    c: PointOnObject(g49,g44)
    c: Horizontal(g49)
    c: Coincident(g50,g49)
    c: PointOnObject(g50,g43)
    c: Horizontal(g50)
    c: Distance(g51) = 30
    c: Horizontal(g51)
    c: Coincident(g51,g42)
    c: Coincident(g52,g51)
    c: Coincident(g52,g46)
    c: Symmetric(g52,g52,g53)
    c: PointOnObject(g53,g44)
    c: Horizontal(g53)
    c: Coincident(g54,g53)
    c: PointOnObject(g54,g43)
    c: Horizontal(g54)
    c: Distance(g55) = 5
    c: Coincident(g55,g54)
    c: PointOnObject(g55,g54)
    c: Coincident(g56,g55)
    c: PointOnObject(g56,g45)
    c: Vertical(g56)
    c: Coincident(g57,g56)
    c: PointOnObject(g57,g50)
    c: Vertical(g57)
    c: Distance(g58) = 5
    c: Coincident(g58,g53)
    c: PointOnObject(g58,g54)
    c: Coincident(g59,g58)
    c: PointOnObject(g59,g45)
    c: Vertical(g59)
    c: Coincident(g60,g59)
    c: PointOnObject(g60,g50)
    c: Vertical(g60)
    c: Coincident(g61,g55)
    c: Diameter(g61) = 3
    c: Coincident(g62,g58)
    c: Equal(g61,g62)
    c: Coincident(g63,g56)
    c: Equal(g61,g63)
    c: Coincident(g64,g59)
    c: Equal(g63,g64)
    c: Coincident(g65,g57)
    c: Equal(g63,g65)
    c: Coincident(g66,g60)
    c: Equal(g65,g66)
    c: DistanceY(g41,g28) = 37.9999
FEATURE [PartDesign::Pad] Pad002
  Direction = (0,0,1)
  Length = 4
  Length2 = 10
  Profile = -> Sketch002
  ReferenceAxis = -> Sketch002 [N_Axis]
  Refine = true
  Suppressed = false
  Type = 0
FEATURE [PartDesign::Body] Body004  label="arm_low_002"
  AllowCompound = false
  Group = -> [Sketch002,Pad002]
  Origin = -> Origin004
  Placement = pos=(0,0,77.3) rot=(0,0,1;0.013804rad)
  Tip = -> Pad002
COMPONENT P5 — recipe-attached ("arm_high_002", modeled in this document).
Construction recipe (the document's own serialized feature program — sketch geometry with constraints, then the solid features built on it; lengths are millimeters unless a unit is written):

FEATURE [Sketcher::SketchObject] Sketch003
  ArcFitTolerance = 1e-06
  FullyConstrained = false
  MakeInternals = false
  MapMode = 5
  sketch-geometry (41):
    g0: Circle [constr] CenterX=7e-16 CenterY=0.000303 CenterZ=0 NormalX=0 NormalY=0 NormalZ=1 AngleXU=0 Radius=14
    g1: LineSegment [constr] StartX=7e-16 StartY=0.000303 StartZ=0 EndX=7e-16 EndY=400.001 EndZ=0
    g2: Circle CenterX=7e-16 CenterY=400.001 CenterZ=0 NormalX=0 NormalY=0 NormalZ=1 AngleXU=0 Radius=5
    g3: Circle CenterX=7e-16 CenterY=0 CenterZ=0 NormalX=0 NormalY=0 NormalZ=1 AngleXU=0 Radius=5
    g4: Circle CenterX=7e-16 CenterY=400.001 CenterZ=0 NormalX=0 NormalY=0 NormalZ=1 AngleXU=0 Radius=2
    g5: Circle CenterX=7e-16 CenterY=0.000303 CenterZ=0 NormalX=0 NormalY=0 NormalZ=1 AngleXU=0 Radius=2
    g6: Circle [constr] CenterX=0 CenterY=0 CenterZ=0 NormalX=0 NormalY=0 NormalZ=1 AngleXU=0 Radius=11
    g7: ArcOfCircle CenterX=7e-16 CenterY=0 CenterZ=0 NormalX=0 NormalY=0 NormalZ=1 AngleXU=0 Radius=25 StartAngle=3.14159 EndAngle=6.28319
    g8: ArcOfCircle CenterX=7e-16 CenterY=400.001 CenterZ=0 NormalX=0 NormalY=0 NormalZ=1 AngleXU=0 Radius=25 StartAngle=6e-16 EndAngle=3.14159
    g9: LineSegment StartX=-25 StartY=-8e-15 StartZ=0 EndX=-25 EndY=400.001 EndZ=0
    g10: LineSegment StartX=25 StartY=0 StartZ=0 EndX=25 EndY=400.001 EndZ=0
    g11: Circle CenterX=10.9997 CenterY=400.001 CenterZ=0 NormalX=0 NormalY=0 NormalZ=1 AngleXU=0 Radius=1.25
    g12: Circle CenterX=0 CenterY=411.001 CenterZ=0 NormalX=0 NormalY=0 NormalZ=1 AngleXU=0 Radius=1.25
    g13: Circle CenterX=-10.9997 CenterY=400.001 CenterZ=0 NormalX=0 NormalY=0 NormalZ=1 AngleXU=0 Radius=1.25
    g14: Circle CenterX=0 CenterY=389.001 CenterZ=0 NormalX=0 NormalY=0 NormalZ=1 AngleXU=0 Radius=1.25
    g15: Circle CenterX=10.9997 CenterY=0.000303 CenterZ=0 NormalX=0 NormalY=0 NormalZ=1 AngleXU=0 Radius=1.25
    g16: Circle CenterX=0 CenterY=11 CenterZ=0 NormalX=0 NormalY=0 NormalZ=1 AngleXU=0 Radius=1.25
    g17: Circle CenterX=-10.9997 CenterY=0.000303 CenterZ=0 NormalX=0 NormalY=0 NormalZ=1 AngleXU=0 Radius=1.25
    g18: Circle CenterX=0 CenterY=-10.9994 CenterZ=0 NormalX=0 NormalY=0 NormalZ=1 AngleXU=0 Radius=1.25
    g19: LineSegment [constr] StartX=25 StartY=200 StartZ=0 EndX=-25 EndY=200 EndZ=0
    g20: LineSegment [constr] StartX=25 StartY=200 StartZ=0 EndX=55 EndY=200 EndZ=0
    g21: LineSegment [constr] StartX=25 StartY=0 StartZ=0 EndX=55 EndY=0 EndZ=0
    g22: LineSegment [constr] StartX=25 StartY=400.001 StartZ=0 EndX=55 EndY=400.001 EndZ=0
    g23: LineSegment [constr] StartX=55 StartY=200 StartZ=0 EndX=55 EndY=400.001 EndZ=0
    g24: LineSegment [constr] StartX=55 StartY=200 StartZ=0 EndX=55 EndY=0 EndZ=0
    g25: LineSegment [constr] StartX=55 StartY=100 StartZ=0 EndX=25 EndY=100 EndZ=0
    g26: LineSegment [constr] StartX=25 StartY=100 StartZ=0 EndX=-25 EndY=100 EndZ=0
    g27: LineSegment [constr] StartX=55 StartY=300 StartZ=0 EndX=25 EndY=300 EndZ=0
    g28: LineSegment [constr] StartX=25 StartY=300 StartZ=0 EndX=-25 EndY=300 EndZ=0
    g29: LineSegment [constr] StartX=-25 StartY=300 StartZ=0 EndX=-20 EndY=300 EndZ=0
    g30: LineSegment [constr] StartX=-20 StartY=300 StartZ=0 EndX=-20 EndY=200 EndZ=0
    g31: LineSegment [constr] StartX=-20 StartY=200 StartZ=0 EndX=-20 EndY=100 EndZ=0
    g32: LineSegment [constr] StartX=25 StartY=100 StartZ=0 EndX=20 EndY=100 EndZ=0
    g33: LineSegment [constr] StartX=20 StartY=100 StartZ=0 EndX=20 EndY=200 EndZ=0
    g34: LineSegment [constr] StartX=20 StartY=200 StartZ=0 EndX=20 EndY=300 EndZ=0
    g35: Circle CenterX=-20 CenterY=300 CenterZ=0 NormalX=0 NormalY=0 NormalZ=1 AngleXU=0 Radius=1.5
    g36: Circle CenterX=20 CenterY=300 CenterZ=0 NormalX=0 NormalY=0 NormalZ=1 AngleXU=0 Radius=1.5
    g37: Circle CenterX=-20 CenterY=200 CenterZ=0 NormalX=0 NormalY=0 NormalZ=1 AngleXU=0 Radius=1.5
    g38: Circle CenterX=20 CenterY=200 CenterZ=0 NormalX=0 NormalY=0 NormalZ=1 AngleXU=0 Radius=1.5
    g39: Circle CenterX=-20 CenterY=100 CenterZ=0 NormalX=0 NormalY=0 NormalZ=1 AngleXU=0 Radius=1.5
    g40: Circle CenterX=20 CenterY=100 CenterZ=0 NormalX=0 NormalY=0 NormalZ=1 AngleXU=0 Radius=1.5
  constraints (85):
    c: Diameter(g0) = 28
    c: Coincident(g1,g0)
    c: Vertical(g1)
    c: Coincident(g2,g1)
    c: Diameter(g3) = 10
    c: Diameter(g4) = 4
    c: Coincident(g4,g1)
    c: Diameter(g5) = 4
    c: Coincident(g5,g0)
    c: Diameter(g6) = 22
    c: Tangent(g7,g9) = 1.5708
    c: Tangent(g7,g10) = -1.5708
    c: Tangent(g8,g9) = 1.5708
    c: Tangent(g8,g10) = -1.5708
    c: Equal(g7,g8)
    c: Radius(g7) = 25
    c: Coincident(g7,g3)
    c: Coincident(g8,g1)
    c: Vertical(g9)
    c: Diameter(g12) = 2.5
    c: Diameter(g13) = 2.5
    c: Diameter(g14) = 2.5
    c: Diameter(g11) = 2.5
    c: Diameter(g16) = 2.5
    c: Diameter(g17) = 2.5
    c: Diameter(g18) = 2.5
    c: Diameter(g15) = 2.5
    c: Symmetric(g10,g10,g19)
    c: Symmetric(g9,g9,g19)
    c: Distance(g20) = 30
    c: Horizontal(g20)
    c: Coincident(g20,g19)
    c: Distance(g21) = 30
    c: Horizontal(g21)
    c: Coincident(g21,g7)
    c: PointOnObject(g21,g-1)
    c: Distance(g22) = 30
    c: Horizontal(g22)
    c: Coincident(g22,g8)
    c: Coincident(g23,g20)
    c: Coincident(g23,g22)
    c: Coincident(g24,g20)
    c: Coincident(g24,g21)
    c: Symmetric(g24,g24,g25)
    c: PointOnObject(g25,g10)
    c: Horizontal(g25)
    c: Coincident(g26,g25)
    c: PointOnObject(g26,g9)
    c: Horizontal(g26)
    c: Symmetric(g23,g23,g27)
    c: PointOnObject(g27,g10)
    c: Horizontal(g27)
    c: Coincident(g28,g27)
    c: PointOnObject(g28,g9)
    c: Horizontal(g28)
    c: Distance(g29) = 5
    c: Horizontal(g29)
    c: Coincident(g29,g28)
    c: Coincident(g30,g29)
    c: PointOnObject(g30,g19)
    c: Vertical(g30)
    c: Coincident(g31,g30)
    c: PointOnObject(g31,g26)
    c: Vertical(g31)
    c: Distance(g32) = 5
    c: Horizontal(g32)
    c: Coincident(g32,g25)
    c: Coincident(g33,g32)
    c: PointOnObject(g33,g19)
    c: Vertical(g33)
    c: Coincident(g34,g33)
    c: PointOnObject(g34,g28)
    c: Vertical(g34)
    c: Diameter(g35) = 3
    c: Coincident(g35,g29)
    c: Coincident(g36,g34)
    c: Equal(g35,g36)
    c: Coincident(g37,g30)
    c: Equal(g35,g37)
    c: Coincident(g38,g33)
    c: Equal(g37,g38)
    c: Coincident(g39,g31)
    c: Equal(g37,g39)
    c: Coincident(g40,g32)
    c: Equal(g39,g40)
FEATURE [PartDesign::Pad] Pad003
  Direction = (0,0,1)
  Length = 4
  Length2 = 10
  Profile = -> Sketch003
  ReferenceAxis = -> Sketch003 [N_Axis]
  Refine = true
  Suppressed = false
  Type = 0
FEATURE [PartDesign::Body] Body005  label="arm_high_002"
  AllowCompound = false
  Group = -> [Sketch003,Pad003]
  Origin = -> Origin005
  Placement = pos=(387.832,472.58,73.3) rot=(0,0,1;1.75335rad)
  Tip = -> Pad003
COMPONENT P6 — same part as P0; its construction recipe is shown at P0.
COMPONENT P7 — same part as P0; its construction recipe is shown at P0.
COMPONENT P8 — same part as P1; its construction recipe is shown at P1.
COMPONENT P9 — same part as P1; its construction recipe is shown at P1.
COMPONENT P10 — geometry summary ("DC05_M01_DUMMY"; no construction recipe available for this part):
  bounding box: 62.1 x 50.0 x 40.2 mm
  tessellated surface: 15,944 triangles
  volume: 72104 mm^3 (58% of its bounding box)
  symmetry: mirror-symmetric across its x mid-plane
COMPONENT P11 — geometry summary ("DC05_M01_DUMMY001"; no construction recipe available for this part):
  bounding box: 62.3 x 50.0 x 40.8 mm
  tessellated surface: 15,944 triangles
  volume: 72104 mm^3 (57% of its bounding box)
  symmetry: mirror-symmetric across its x mid-plane
COMPONENT P12 — geometry summary ("DC05_M01_DUMMY002"; no construction recipe available for this part):
  bounding box: 62.1 x 50.0 x 40.2 mm
  tessellated surface: 15,944 triangles
  volume: 72104 mm^3 (58% of its bounding box)
  symmetry: mirror-symmetric across its x mid-plane
COMPONENT P13 — geometry summary ("DC05_M01_DUMMY003"; no construction recipe available for this part):
  bounding box: 62.3 x 50.0 x 40.8 mm
  tessellated surface: 15,944 triangles
  volume: 72104 mm^3 (57% of its bounding box)
  symmetry: mirror-symmetric across its x mid-plane
PROVENANCE & LICENSES
A FreeCAD (.FCStd) document from a public repository crawl; recipes are the document's own serialized feature recipes (and, for linked parts, companion documents' recipes).
License: unknown-license-file.
